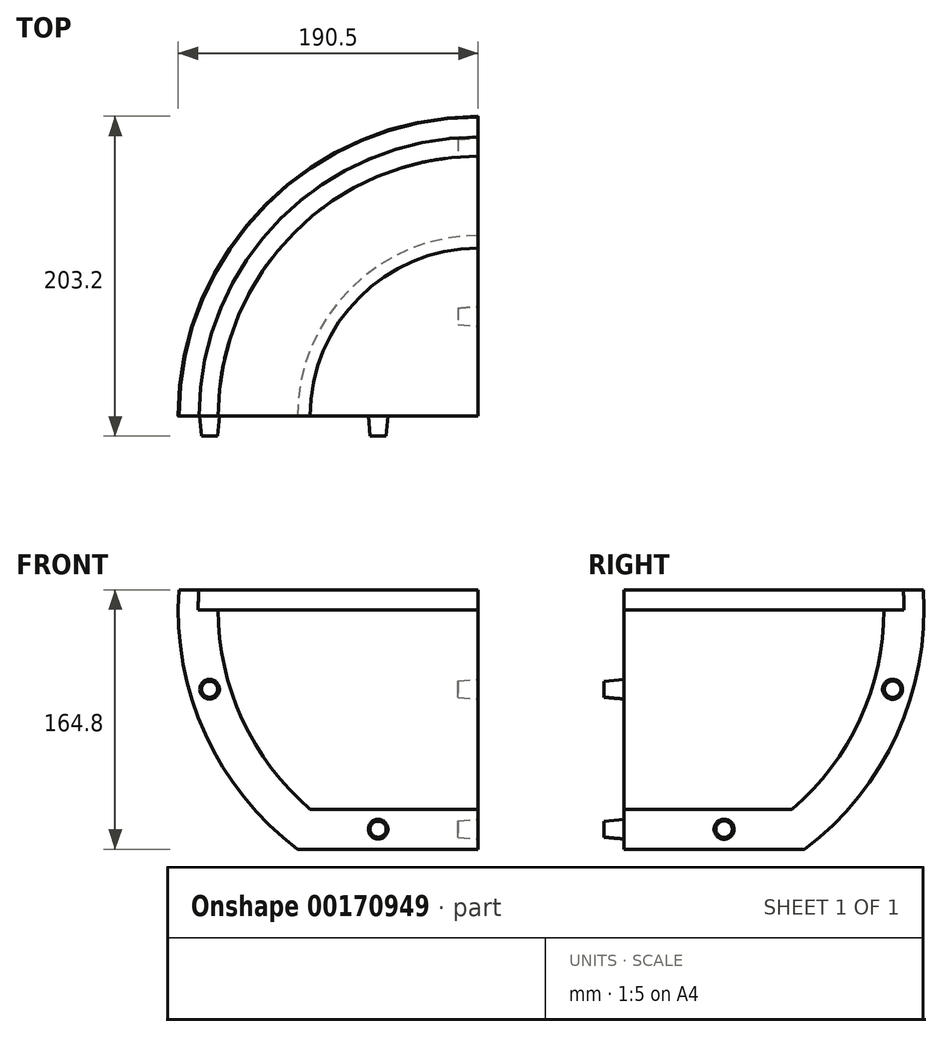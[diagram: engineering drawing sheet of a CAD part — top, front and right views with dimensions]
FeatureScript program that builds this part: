
annotation { "Feature Type Name" : "Feature", "Feature Type Description" : "" }
export const myFeature = defineFeature(function(context is Context, id is Id, definition is map)
    precondition{}
    {
        {
            var Q0;
            Q0=qCreatedBy(makeId("Front.planeOp"),FACE);
            var sketch = newSketch(context, id + "F0", { "sketchPlane" : qUnion([Q0])});
            skLineSegment(sketch, "E0", {"start": v(-177.35, 12.7) * mm, "end": v(-177.35, 12.7) * mm});
            skArc(sketch, "E1", {"start": v(-177.35, 12.7) * mm, "mid": v(-177.69, 6.35) * mm, "end": v(-177.8, 0) * mm});
            skLineSegment(sketch, "E2", {"start": v(-165.1, 0) * mm, "end": v(-177.8, 0) * mm});
            skLineSegment(sketch, "E3", {"start": v(-114.7, -152.1) * mm, "end": v(0, -152.1) * mm});
            skLineSegment(sketch, "E4", {"start": v(0, -126.7) * mm, "end": v(0, -152.1) * mm});
            skArc(sketch, "E5", {"start": v(-165.1, 0) * mm, "mid": v(-149.82, -69.75) * mm, "end": v(-106.74, -126.7) * mm});
            skLineSegment(sketch, "E6", {"start": v(0, -126.7) * mm, "end": v(-106.74, -126.7) * mm});
            skArc(sketch, "E7", {"start": v(-190.08, 12.7) * mm, "mid": v(-173.24, -79.24) * mm, "end": v(-114.7, -152.1) * mm});
            skLineSegment(sketch, "E8", {"start": v(-190.08, 12.7) * mm, "end": v(-177.35, 12.7) * mm});
            skSolve(sketch);
        }
        {
            var Q0;
            Q0=makeQuery(id+"F0.imprint","IMPRINT",FACE,{"disambiguationData":[TD([[makeQuery(id+"F0.imprint","IMPRINT",EDGE,{"derivedFrom":sQuery(id+"F0.wireOp",EDGE,"E1")}),-1.0]])]});
            var Q1;
            Q1=sQuery(id+"F0.wireOp",EDGE,"E4");
            revolve(context, id + "F1", {"entities" : qUnion([Q0]), "axis" : qUnion([Q1]), "revolveType" : RevolveType.ONE_DIRECTION, "angle" : 90 * degree});
        }
        {
            var Q0;
            Q0=makeQuery(id+"F0.imprint","IMPRINT",FACE,{"disambiguationData":[TD([[makeQuery(id+"F0.imprint","IMPRINT",EDGE,{"derivedFrom":sQuery(id+"F0.wireOp",EDGE,"E1")}),-1.0]])]});
            var sketch = newSketch(context, id + "F2", { "sketchPlane" : qUnion([Q0])});
            skCircle(sketch, "E9", {"center": v(-170.55, -50.5) * mm, "radius": 6.22 * mm});
            skCircle(sketch, "E10", {"center": v(-63.5, -139.4) * mm, "radius": 6.22 * mm});
            skSolve(sketch);
        }
        {
            var Q0;
            Q0=qSketchRegion(id+"F2",true);
            extrude(context, id + "F3", {"entities" : qUnion([Q0]), "operationType" : NewBodyOperationType.ADD, "depth" : 12.7 * mm, "hasDraft" : true, "draftAngle" : 5 * degree, "draftPullDirection" : true});
        }
        {
            var Q0;
            Q0=makeQuery(id+"F1.opRevolve","CAP_FACE",FACE,{"disambiguationData":[OSD([sQuery(id+"F0.wireOp",EDGE,"52e400c0-8d15-4c76-a6e8-97da84b9dea01"),sQuery(id+"F0.wireOp",EDGE,"c329610f-a132-4cbf-8fab-355534a813d1"),sQuery(id+"F0.wireOp",EDGE,"y3XLxCqT-Zuhn-f9uB-kABT-CfS1m2HE6Dtt"),sQuery(id+"F0.wireOp",EDGE,"E1"),sQuery(id+"F0.wireOp",EDGE,"E2"),sQuery(id+"F0.wireOp",EDGE,"IzXMlpwB-L7sk-yMcw-xoRI-lU3HIr0pnRP3"),sQuery(id+"F0.wireOp",EDGE,"ne1X0Thx-fO3S-bZUy-CAni-h6XMJ8rFbJ7e"),sQuery(id+"F0.wireOp",EDGE,"RSa53lpD-toCp-bpwY-JniG-mJgBw1SofFhp"),sQuery(id+"F0.wireOp",EDGE,"e5ad18b1-49db-4535-918d-1c280957c938")])],"isStart":false});
            var sketch = newSketch(context, id + "F4", { "sketchPlane" : qUnion([Q0])});
            skCircle(sketch, "E11", {"center": v(170.55, -50.5) * mm, "radius": 6.35 * mm});
            skCircle(sketch, "E12", {"center": v(63.5, -139.4) * mm, "radius": 6.35 * mm});
            skSolve(sketch);
        }
        {
            var Q0;
            Q0=qSketchRegion(id+"F4",true);
            extrude(context, id + "F5", {"entities" : qUnion([Q0]), "operationType" : NewBodyOperationType.REMOVE, "oppositeDirection" : true, "depth" : 12.7 * mm, "hasDraft" : true, "draftAngle" : 5 * degree, "draftPullDirection" : true});
        }
    });
